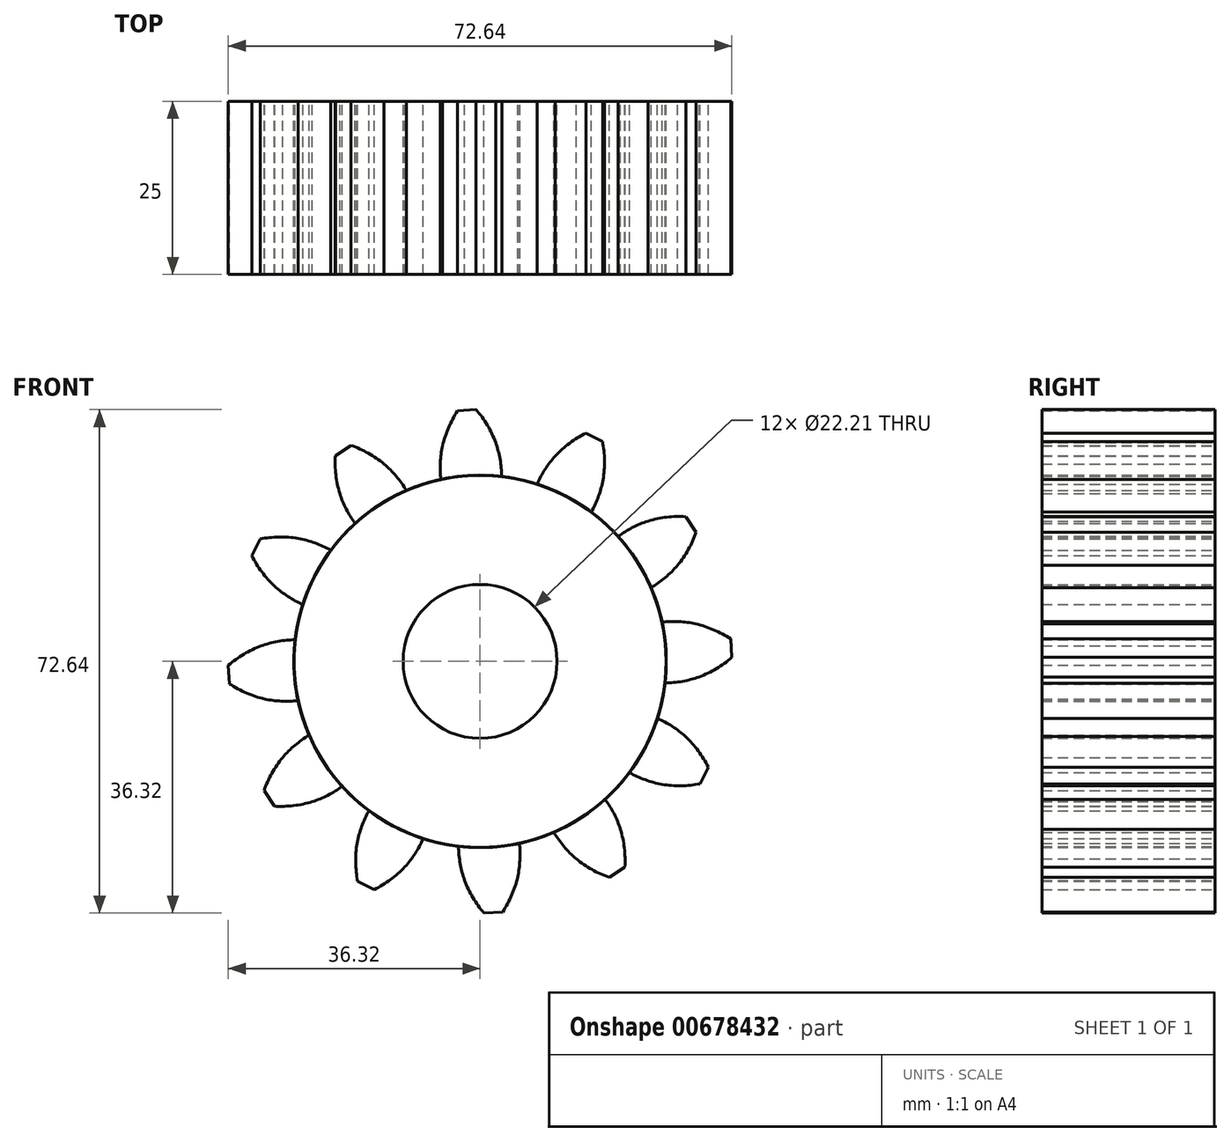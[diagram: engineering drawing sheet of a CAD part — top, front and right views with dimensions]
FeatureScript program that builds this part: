
annotation { "Feature Type Name" : "Feature", "Feature Type Description" : "" }
export const myFeature = defineFeature(function(context is Context, id is Id, definition is map)
    precondition{}
    {
        {
            var Q0;
            Q0=qCreatedBy(makeId("Front.planeOp"),FACE);
            var sketch = newSketch(context, id + "F0", { "sketchPlane" : qUnion([Q0])});
            skCircle(sketch, "E0", {"center": v(0, 0) * mm, "radius": 26.86 * mm});
            skCircle(sketch, "E1", {"center": v(0, 0) * mm, "radius": 29.34 * mm, "construction": true});
            skCircle(sketch, "E2", {"center": v(0, 0) * mm, "radius": 31.75 * mm, "construction": true});
            skArc(sketch, "E3", {"start": v(3.12, 26.6) * mm, "mid": v(2.89, 29.13) * mm, "end": v(2.24, 31.6) * mm});
            skArc(sketch, "E4", {"start": v(2.24, 31.6) * mm, "mid": v(1.04, 34.08) * mm, "end": v(-0.57, 36.32) * mm});
            skArc(sketch, "E5.MirrorCS", {"start": v(-5.42, 31.1) * mm, "mid": v(-4.56, 33.72) * mm, "end": v(-3.25, 36.14) * mm});
            skArc(sketch, "E6.MirrorCS", {"start": v(-5.64, 26.02) * mm, "mid": v(-5.74, 28.57) * mm, "end": v(-5.42, 31.1) * mm});
            skLineSegment(sketch, "E7", {"start": v(-3.25, 36.14) * mm, "end": v(-0.57, 36.32) * mm});
            skCircle(sketch, "E8", {"center": v(0, 0) * mm, "radius": 11.1 * mm});
            skSolve(sketch);
        }
        {
            var Q0;
            Q0 = qSketchRegion(id + "F0", true);
            var Q1;
            Q1=makeQuery(id+"F0.imprint","IMPRINT",FACE,{"disambiguationData":[TD([[makeQuery(id+"F0.imprint","IMPRINT",EDGE,{"derivedFrom":sQuery(id+"F0.wireOp",EDGE,"E0")}),1.0]])]});
            extrude(context, id + "F1", {"entities" : qUnion([Q0, Q1]), "depth" : 25 * mm, "offsetDistance" : 25 * mm});
        }
        {
            var Q0;
            Q0=makeQuery(id+"F1.opExtrude","SWEPT_BODY",BODY,{"disambiguationData":[OSD([sQuery(id+"F0.wireOp",EDGE,"E0"),sQuery(id+"F0.wireOp",EDGE,"E3"),sQuery(id+"F0.wireOp",EDGE,"E4"),sQuery(id+"F0.wireOp",EDGE,"E5.MirrorCS"),sQuery(id+"F0.wireOp",EDGE,"E6.MirrorCS"),sQuery(id+"F0.wireOp",EDGE,"E7")])]});
            var Q1;
            Q1=makeQuery(id+"F1.opExtrude","SWEPT_FACE",FACE,{"disambiguationData":[OSD([sQuery(id+"F0.wireOp",EDGE,"E0")])]});
            circularPattern(context, id + "F2", {"entities" : qUnion([Q0]), "axis" : qUnion([Q1]), "angle" : 360 * degree, "instanceCount" : 12, "equalSpace" : true});
        }
    });
